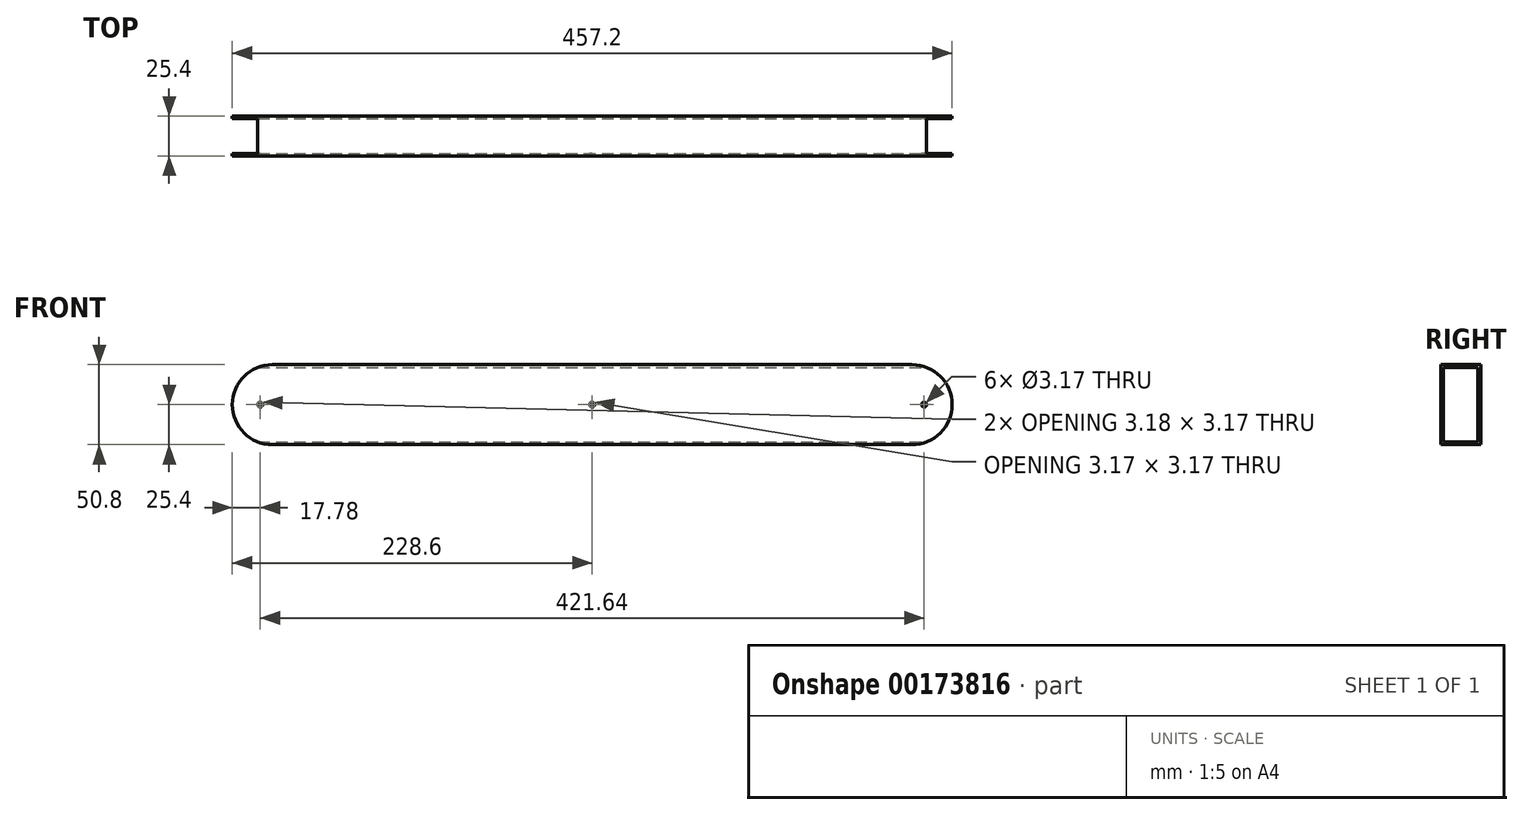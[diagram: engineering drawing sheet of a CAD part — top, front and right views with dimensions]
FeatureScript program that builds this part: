
annotation { "Feature Type Name" : "Feature", "Feature Type Description" : "" }
export const myFeature = defineFeature(function(context is Context, id is Id, definition is map)
    precondition{}
    {
        {
            var Q0;
            Q0=qCreatedBy(makeId("Right.planeOp"),FACE);
            var sketch = newSketch(context, id + "F0", { "sketchPlane" : qUnion([Q0])});
            skLineSegment(sketch, "E0.bottom", {"start": v(-12.7, -25.4) * mm, "end": v(12.7, -25.4) * mm});
            skLineSegment(sketch, "E0.top", {"start": v(-12.7, 25.4) * mm, "end": v(12.7, 25.4) * mm});
            skLineSegment(sketch, "E0.left", {"start": v(-12.7, -25.4) * mm, "end": v(-12.7, 25.4) * mm});
            skLineSegment(sketch, "E0.right", {"start": v(12.7, -25.4) * mm, "end": v(12.7, 25.4) * mm});
            skPoint(sketch, "E0.middle", {"position": v(0, 0) * mm});
            skSolve(sketch);
        }
        {
            var Q0;
            Q0=makeQuery(id+"F0.imprint","IMPRINT",FACE,{"disambiguationData":[TD([[makeQuery(id+"F0.imprint","IMPRINT",EDGE,{"derivedFrom":sQuery(id+"F0.wireOp",EDGE,"E0.bottom")}),1.0]])]});
            extrude(context, id + "F1", {"entities" : qUnion([Q0]), "endBound" : BoundingType.SYMMETRIC, "depth" : 457.2 * mm});
        }
        {
            var Q0;
            Q0=makeQuery(id+"F1.opExtrude","CAP_FACE",FACE,{"disambiguationData":[OSD([sQuery(id+"F0.wireOp",EDGE,"E0.bottom"),sQuery(id+"F0.wireOp",EDGE,"E0.top"),sQuery(id+"F0.wireOp",EDGE,"E0.left"),sQuery(id+"F0.wireOp",EDGE,"E0.right")])],"isStart":false});
            var sketch = newSketch(context, id + "F2", { "sketchPlane" : qUnion([Q0])});
            skLineSegment(sketch, "E1.bottom", {"start": v(10.99, -23.69) * mm, "end": v(-10.99, -23.69) * mm});
            skLineSegment(sketch, "E1.top", {"start": v(10.99, 23.69) * mm, "end": v(-10.99, 23.69) * mm});
            skLineSegment(sketch, "E1.left", {"start": v(10.99, -23.69) * mm, "end": v(10.99, 23.69) * mm});
            skLineSegment(sketch, "E1.right", {"start": v(-10.99, -23.69) * mm, "end": v(-10.99, 23.69) * mm});
            skPoint(sketch, "E1.middle", {"position": v(0, 0) * mm});
            skSolve(sketch);
        }
        {
            var Q0;
            Q0=makeQuery(id+"F2.imprint","IMPRINT",FACE,{"disambiguationData":[TD([[makeQuery(id+"F2.imprint","IMPRINT",EDGE,{"derivedFrom":sQuery(id+"F2.wireOp",EDGE,"E1.bottom")}),-1.0]])]});
            extrude(context, id + "F3", {"entities" : qUnion([Q0]), "operationType" : NewBodyOperationType.REMOVE, "endBound" : BoundingType.THROUGH_ALL, "oppositeDirection" : true, "depth" : 25.4 * mm});
        }
        {
            var Q0;
            Q0=makeQuery(id+"F1.opExtrude","SWEPT_FACE",FACE,{"disambiguationData":[OSD([sQuery(id+"F0.wireOp",EDGE,"E0.left")])]});
            var sketch = newSketch(context, id + "F4", { "sketchPlane" : qUnion([Q0])});
            skCircle(sketch, "E2", {"center": v(-210.82, 0) * mm, "radius": 1.59 * mm});
            skCircle(sketch, "E3", {"center": v(0, 0) * mm, "radius": 1.59 * mm});
            skSolve(sketch);
        }
        {
            var Q0;
            Q0 = qSketchRegion(id + "F4", true);
            extrude(context, id + "F5", {"entities" : qUnion([Q0]), "operationType" : NewBodyOperationType.REMOVE, "endBound" : BoundingType.THROUGH_ALL, "oppositeDirection" : true, "depth" : 25.4 * mm});
        }
        {
            var Q0;
            Q0=makeQuery(id+"F4.imprint","IMPRINT",FACE,{"disambiguationData":[TD([[makeQuery(id+"F4.imprint","IMPRINT",EDGE,{"derivedFrom":sQuery(id+"F4.wireOp",EDGE,"E2")}),-1.0]])]});
            var sketch = newSketch(context, id + "F6", { "sketchPlane" : qUnion([Q0])});
            skCircle(sketch, "E4", {"center": v(210.82, 0) * mm, "radius": 1.59 * mm});
            skSolve(sketch);
        }
        {
            var Q0;
            Q0 = qSketchRegion(id + "F6", true);
            extrude(context, id + "F7", {"entities" : qUnion([Q0]), "operationType" : NewBodyOperationType.REMOVE, "endBound" : BoundingType.THROUGH_ALL, "oppositeDirection" : true, "depth" : 25.4 * mm});
        }
        {
            var Q0;
            Q0=makeQuery(id+"F1.opExtrude","CAP_EDGE",EDGE,{"disambiguationData":[OSD([sQuery(id+"F0.wireOp",EDGE,"E0.bottom")])],"isStart":true});
            var Q1;
            Q1=makeQuery(id+"F1.opExtrude","CAP_EDGE",EDGE,{"disambiguationData":[OSD([sQuery(id+"F0.wireOp",EDGE,"E0.top")])],"isStart":true});
            fillet(context, id + "F8", {"entities" : qUnion([Q0, Q1]), "radius" : 25.4 * mm, "tangentPropagation" : true, "allowEdgeOverflow" : false});
        }
        {
            var Q0;
            Q0=makeQuery(id+"F1.opExtrude","CAP_EDGE",EDGE,{"disambiguationData":[OSD([sQuery(id+"F0.wireOp",EDGE,"E0.top")])],"isStart":false});
            var Q1;
            Q1=makeQuery(id+"F1.opExtrude","CAP_EDGE",EDGE,{"disambiguationData":[OSD([sQuery(id+"F0.wireOp",EDGE,"E0.bottom")])],"isStart":false});
            fillet(context, id + "F9", {"entities" : qUnion([Q0, Q1]), "radius" : 25.4 * mm, "tangentPropagation" : true, "allowEdgeOverflow" : false});
        }
    });
